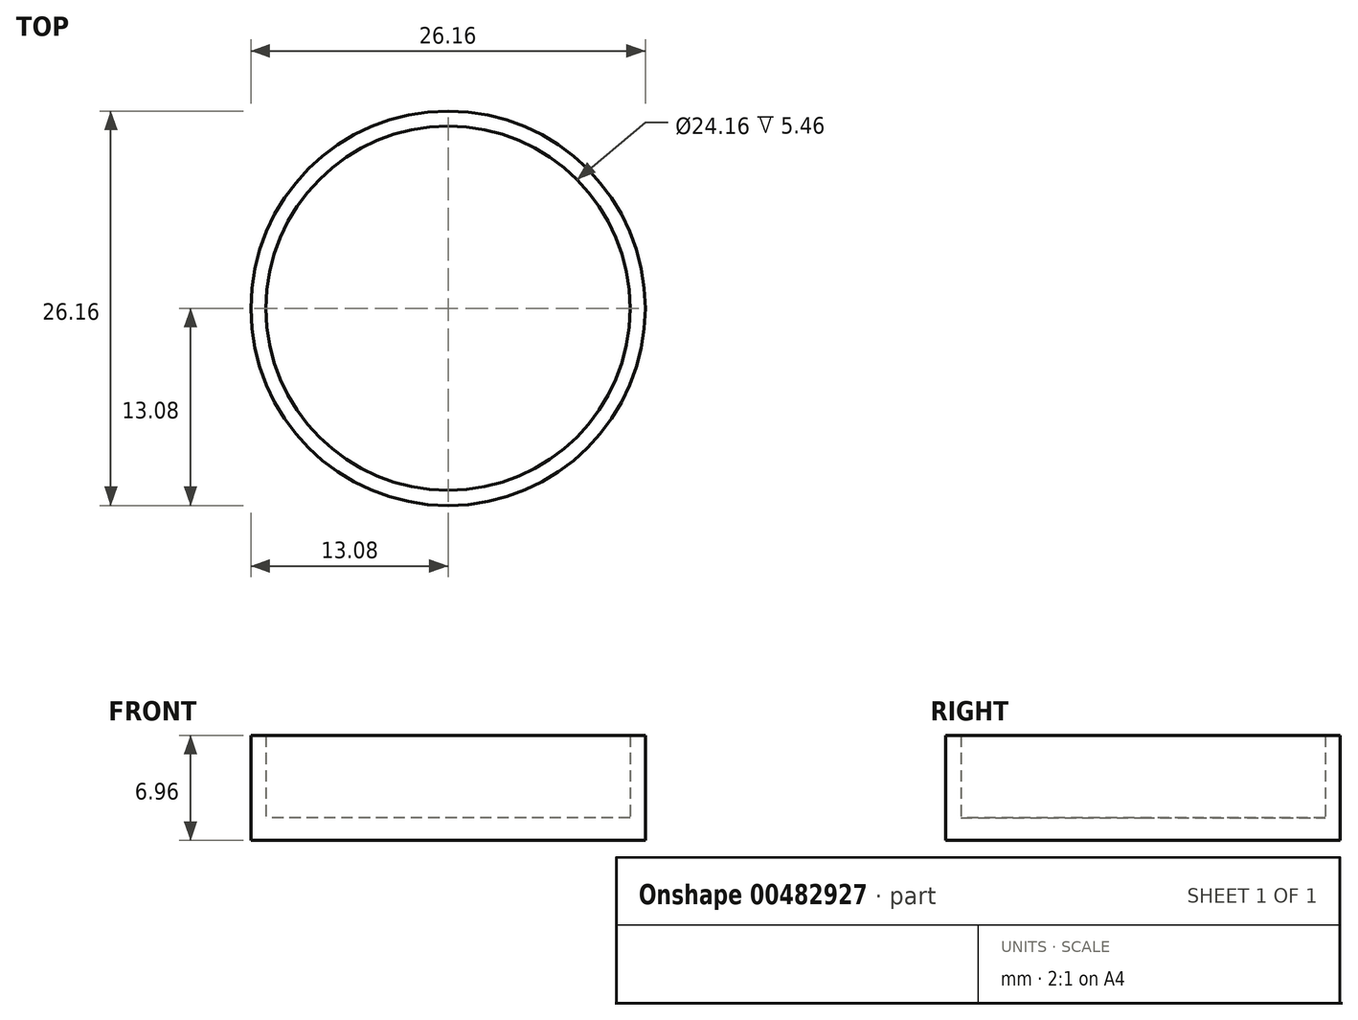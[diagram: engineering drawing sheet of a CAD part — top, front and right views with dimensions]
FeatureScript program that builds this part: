
annotation { "Feature Type Name" : "Feature", "Feature Type Description" : "" }
export const myFeature = defineFeature(function(context is Context, id is Id, definition is map)
    precondition{}
    {
        {
            var Q0;
            Q0=qCreatedBy(makeId("Top.planeOp"),FACE);
            var sketch = newSketch(context, id + "F0", { "sketchPlane" : qUnion([Q0])});
            skCircle(sketch, "E0", {"center": v(0, 0) * mm, "radius": 13.08 * mm});
            skSolve(sketch);
        }
        {
            var Q0;
            Q0 = qSketchRegion(id + "F0", true);
            extrude(context, id + "F1", {"entities" : qUnion([Q0]), "depth" : 1.5 * mm});
        }
        {
            var Q0;
            Q0=makeQuery(id+"F1.opExtrude","CAP_FACE",FACE,{"disambiguationData":[OSD([sQuery(id+"F0.wireOp",EDGE,"E0")])],"isStart":false});
            var sketch = newSketch(context, id + "F2", { "sketchPlane" : qUnion([Q0])});
            skCircle(sketch, "E1.0", {"center": v(0, 0) * mm, "radius": 12.08 * mm});
            skCircle(sketch, "E2", {"center": v(0, 0) * mm, "radius": 13.08 * mm});
            skSolve(sketch);
        }
        {
            var Q0;
            Q0 = qSketchRegion(id + "F2", true);
            extrude(context, id + "F3", {"entities" : qUnion([Q0]), "operationType" : NewBodyOperationType.ADD, "depth" : 6.96 * mm - 1.5 * mm, "offsetDistance" : 25.4 * mm});
        }
    });
